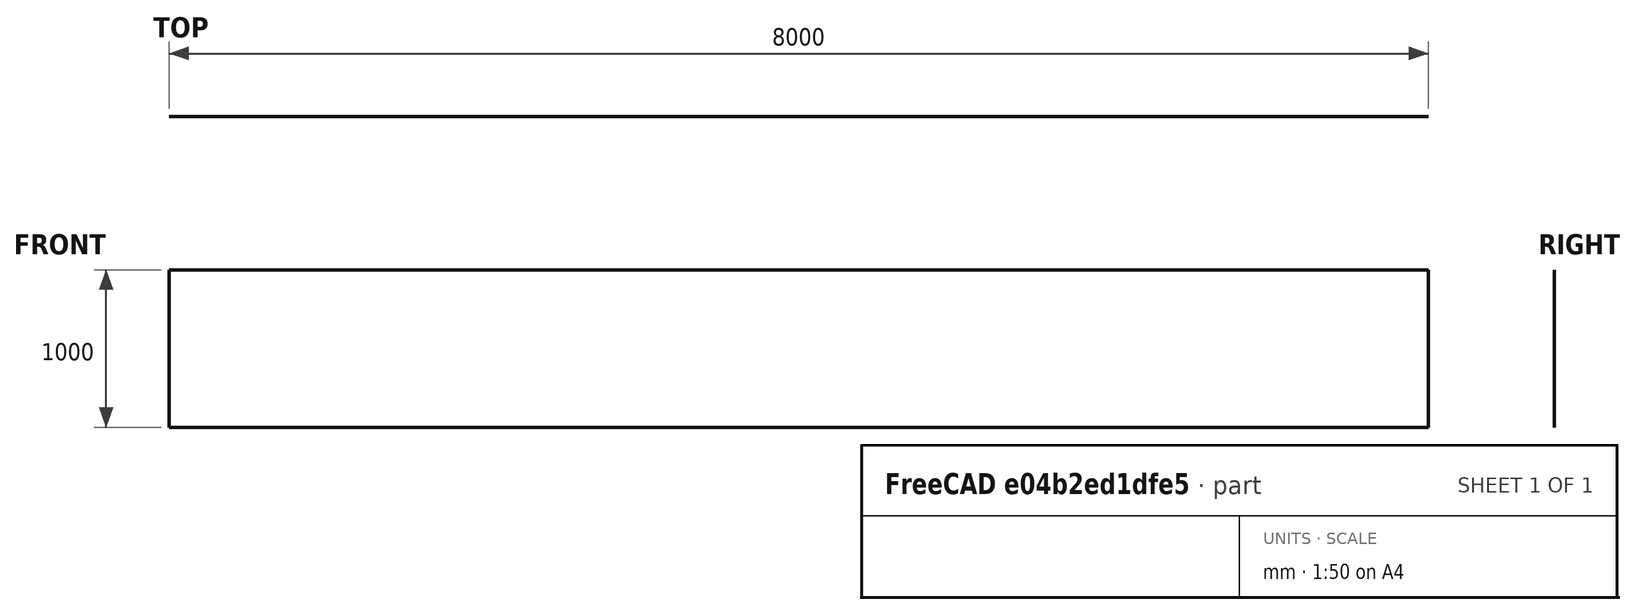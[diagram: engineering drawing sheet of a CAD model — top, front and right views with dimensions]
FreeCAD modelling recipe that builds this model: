
FCSTD DOCUMENT  (FreeCAD 0.19R20224 (Git))
Label: FemCalculixCantilever2D
License: CC-BY 3.0
LicenseURL: http://creativecommons.org/licenses/by/3.0/
objects: Fem::FemMeshObjectPython×2, Part::Plane×1, Fem::FemSolverObjectPython×1, Fem::ConstraintFixed×1, Fem::ConstraintForce×1, Fem::FemPostWarpVectorFilter×1, Fem::FemPostPipeline×1, App::MaterialObjectPython×1, Fem::FeaturePython×1, Fem::FemResultObjectPython×1, Fem::FemAnalysis×1
note: 1 computed .brp shape members not serialized (recipe doc carries the construction recipe); baked Part::Feature solids carry a one-line shape summary decoded from their .brp

FEATURE [Part::Plane] Plane
  AttacherType = Attacher::AttachEngine3D
  Length = 8000
  Placement = pos=(0,500,0) rot=(1,0,0;1.5708rad)
  Width = 1000
FEATURE [Fem::FemMeshObjectPython] FEMMeshGmsh  # FEM object (typed FeaturePython)
  Algorithm2D = 0
  Algorithm3D = 0
  CharacteristicLengthMax = 500
  CharacteristicLengthMin = 0
  CoherenceMesh = true
  ElementDimension = 0
  ElementOrder = 1
  GeometryTolerance = 1e-06
  GroupsOfNodes = false
  HighOrderOptimize = false
  OptimizeNetgen = false
  OptimizeStd = true
  Part = -> Plane
  RecombineAll = false
FEATURE [Fem::FemSolverObjectPython] CalculiXccxTools  # FEM object (typed FeaturePython)
  AnalysisType = 0
  BeamShellResultOutput3D = false
  EigenmodeHighLimit = 0
  EigenmodeLowLimit = 0
  EigenmodesCount = 15
  GeometricalNonlinearity = 0
  IterationsControlParameterCutb = 0.25,0.5,0.75,0.85,,,1.5,
  IterationsControlParameterIter = 4,8,9,200,10,400,,200,,
  IterationsControlParameterTimeUse = false
  IterationsThermoMechMaximum = 2000
  IterationsUserDefinedIncrementations = false
  IterationsUserDefinedTimeStepLength = false
  MaterialNonlinearity = 0
  MatrixSolverType = 0
  SplitInputWriter = false
  ThermoMechSteadyState = true
  TimeEnd = 1
  TimeInitialStep = 1
FEATURE [Fem::ConstraintFixed] FemConstraintFixed
  NormalDirection = (0,0,1)
  Normals = (4) [(0,0,1),(0,0,1),(0,0,1),(0,0,1)]
  Points = (4) [(0,500,0),(0,500,333.333),(0,500,666.667),(0,500,1000)]
  References = -> [Plane]
  Scale = 33
FEATURE [Fem::ConstraintForce] FemConstraintForce
  Direction = -> Plane [Edge3]
  DirectionVector = (0,0,-1)
  Force = 9000000
  NormalDirection = (0,0,1)
  Points = (4) [(8000,500,0),(8000,500,333.333),(8000,500,666.667),(8000,500,1000)]
  References = -> [Plane]
  Reversed = true
  Scale = 33
FEATURE [Fem::FemPostWarpVectorFilter] WarpVector
  Factor = 31
  Vector = 0
FEATURE [Fem::FemPostPipeline] Pipeline
  Filter = -> [WarpVector]
  Mode = 0
FEATURE [App::MaterialObjectPython] MechanicalSolidMaterial  # material (typed FeaturePython)
  Category = 0
  Material = AuthorAndLicense=CalculiX-Steel,CardName=CalculiX-Steel,Density=7900 kg/m^3,Description=Standard steel material for CalculiX sample calculations,+7 more (map truncated)
FEATURE [Fem::FeaturePython] ElementGeometry2D  # FEM object (typed FeaturePython)
  Thickness = 1000
FEATURE [Fem::FemMeshObjectPython] ResultMesh  # FEM object (typed FeaturePython)
FEATURE [Fem::FemResultObjectPython] CCX_Results  # FEM object (typed FeaturePython)
  DisplacementLengths = [0,0,88.7247,88.7245,0,0,0,1.17213,2.87021,5.321,8.55561,12.5407,17.2233,22.544,28.4407,34.8502,41.7091,48.9533,56.519,64.3418,72.3578,80.5029,0.536992,1.86966,3.92405,6.76804,10.3869,14.7327,19.7474,25.3698,31.537,38.1854,45.2512,52.6705,+143 more]
  DisplacementVectors = (177) [(0,0,0),(0,0,0),(-8.21231,2.93096e-11,-88.3438),(8.21213,3.47633e-11,-88.3436),(0,0,0),(0,0,0),(0,0,0),(-0.977523,-2.66974e-13,-0.646785),+169 more]
  Eigenmode = 0
  EigenmodeFrequency = 0
  MaxShear = [197.531,198.176,5.55593,5.42475,18.4214,92.3422,93.1625,203.084,189.122,175.537,162.02,148.52,135.022,121.524,108.027,94.5312,81.0364,67.5428,54.043,40.5421,26.9911,13.827,204.707,195.603,182.249,168.773,155.269,141.77,128.273,114.776,+147 more]
  Mesh = -> ResultMesh
  NodeNumbers = [1,2,3,4,5,6,7,8,9,10,11,12,13,14,15,16,17,18,19,20,21,22,23,24,25,26,27,28,29,30,31,32,33,34,35,36,37,38,39,40,41,42,43,44,45,46,47,48,49,50,51,52,53,54,55,56,57,58,59,60,61,62,63,64,65,66,67,68,69,+108 more]
  NodeStrainXX = [-0.00188192,0.00188983,-2.69098e-05,2.68924e-05,9.63162e-07,-0.000844443,0.000853696,-0.00190711,-0.00180058,-0.00167161,-0.00154288,-0.00141428,-0.00128571,-0.00115714,-0.00102857,-0.000899997,-0.000771426,-0.000642841,-0.000514185,+158 more]
  NodeStrainXY = [-3.18505e-16,2.26167e-16,1.87061e-17,4.29762e-17,-1.84456e-17,-1.64495e-16,1.05038e-16,-3.3174e-16,-3.16892e-16,-3.16921e-16,-3.1369e-16,-2.75405e-16,-2.27475e-16,-1.94508e-16,-1.83979e-16,-1.39448e-16,-1.04951e-16,-9.97282e-17,+159 more]
  NodeStrainXZ = [-0.000155345,-0.000143245,-2.00024e-05,-1.96262e-05,0.000113937,1.44242e-05,1.8983e-05,3.70454e-05,-1.35021e-05,-1.49882e-05,-1.51533e-05,-1.51452e-05,-1.51444e-05,-1.51447e-05,-1.51447e-05,-1.51445e-05,-1.51446e-05,-1.51454e-05,+159 more]
  NodeStrainYY = [0.000552389,-0.000554245,3.95158e-06,-4.43013e-06,2.16571e-07,0.000298594,-0.000299321,0.000561998,0.000540403,0.0005015,0.000462874,0.000424287,0.000385713,0.000347142,0.00030857,0.000269999,0.000231428,0.000192853,0.000154271,0.000115675,+157 more]
  NodeStrainYZ = [6.35952e-18,6.39002e-18,4.73336e-17,-1.56392e-17,-3.07642e-18,8.94467e-19,3.03577e-18,-5.09067e-19,-1.29392e-18,4.90488e-18,-1.92186e-18,-9.05252e-18,-8.56304e-18,1.5856e-17,-4.80828e-18,-3.13584e-18,-5.37865e-19,-2.44041e-17,2.09008e-17,+158 more]
  NodeStrainZZ = [0.000240456,-0.000252753,2.90487e-05,-2.76071e-05,-8.62973e-06,-1.50263e-09,1.46298e-09,0.00060617,0.000540779,0.000501499,0.000462853,0.000424283,0.000385713,0.000347142,0.00030857,0.000269999,0.000231428,0.000192852,0.000154235,+158 more]
  NodeStressXX = [-435.949,436.468,-3.60908,3.72084,-0.747008,-202.542,205.07,-397.597,-378.019,-351.035,-324.004,-296.999,-269.999,-242.999,-215.999,-188.999,-161.999,-134.997,-107.98,-80.9465,-53.7887,-27.673,-416.464,-390.896,-364.375,-337.497,-310.499,+150 more]
  NodeStressXY = [-5.14506e-11,3.65347e-11,3.02178e-12,6.94231e-12,-2.97944e-12,-2.6572e-11,1.6968e-11,-5.35895e-11,-5.11902e-11,-5.11948e-11,-5.06729e-11,-4.44883e-11,-3.67459e-11,-3.14206e-11,-2.97194e-11,-2.25262e-11,-1.69535e-11,-1.611e-11,-1.17154e-11,+158 more]
  NodeStressXZ = [-25.0941,-23.1396,-3.23116,-3.17039,18.4051,2.33007,3.06648,5.98426,-2.18111,-2.42118,-2.44785,-2.44654,-2.44641,-2.44645,-2.44645,-2.44642,-2.44643,-2.44656,-2.43746,-2.39535,-2.28557,-1.24982,-6.96558,-2.15969,-2.3436,-2.44254,-2.45063,+150 more]
  NodeStressYY = [-42.7141,41.6567,1.37622,-1.33895,-0.867611,-17.8973,18.8131,1.25881,0.138634,0.00636644,0.00201932,0.000468354,2.34723e-05,-6.73436e-06,1.55127e-06,5.01793e-06,-3.17757e-05,0.000140478,0.0018275,0.00654198,-0.00499185,-0.0772041,-12.8917,+154 more]
  NodeStressYZ = [1.02363e-12,1.03029e-12,7.64617e-12,-2.5263e-12,-4.93827e-13,1.42109e-13,4.83169e-13,-8.19345e-14,-2.09038e-13,7.92325e-13,-3.10454e-13,-1.46233e-12,-1.38326e-12,2.56136e-12,-7.76721e-13,-5.06557e-13,-8.68839e-14,-3.9422e-12,3.37628e-12,+158 more]
  NodeStressZZ = [-93.1033,90.3594,5.43037,-5.08293,-2.29663,-66.132,67.1651,8.39427,0.199458,0.00622552,-0.00135391,-5.45392e-05,2.41424e-05,3.28647e-08,-4.87089e-07,-1.5389e-05,-1.99547e-06,-6.95469e-05,-0.00393104,-0.00399062,-0.000375323,-0.858266,+155 more]
  PrincipalMax = [-42.7141,438.008,6.46657,4.74371,16.8996,-17.8973,205.138,8.48246,0.212036,0.0229239,0.0171386,0.0200976,0.0221888,0.0246278,0.027705,0.031646,0.0369344,0.0442551,0.0510644,0.0668335,0.0965682,-0.0772041,-7.16845,0.297657,0.107661,+152 more]
  PrincipalMed = [-91.2763,88.8192,1.37622,-1.33895,-0.867611,-66.0922,67.0969,1.25881,0.138634,0.00636644,0.00201932,0.000468354,2.34723e-05,-6.73436e-06,1.55127e-06,5.01793e-06,-3.17757e-05,0.000140478,0.0018275,0.00654198,-0.00499185,-0.800139,-12.8917,+154 more]
  PrincipalMin = [-437.776,41.6567,-4.64528,-6.1058,-19.9432,-202.582,18.8131,-397.685,-378.032,-351.052,-324.022,-297.019,-270.021,-243.024,-216.027,-189.031,-162.036,-135.041,-108.035,-81.0173,-53.8856,-27.7311,-416.583,-390.908,-364.39,-337.515,-310.518,+150 more]
  ResultType = Fem::ResultMechanical
  Stats = [-8.21231,8.21213,-3.94594e-13,3.47633e-11,-88.3438,0.0121269,0,88.7247,9.41896,406.592,-42.7141,438.008,-91.2763,88.8192,-437.776,41.6567,5.42475,204.707,0,0,0,0,0,0,0,0]
  Time = 0
  vonMises = [373.158,375.001,9.6344,9.41896,31.9135,165.922,167.487,402.604,378.207,351.066,324.032,297.029,270.032,243.036,216.041,189.046,162.054,135.064,108.061,81.054,53.9315,27.2996,406.583,390.807,364.464,337.535,310.529,283.53,256.534,229.538,+147 more]
FEATURE [Fem::FemAnalysis] Analysis
  Group = -> [CalculiXccxTools,MechanicalSolidMaterial,ElementGeometry2D,FemConstraintFixed,FemConstraintForce,FEMMeshGmsh,CCX_Results]
